# Revit family: Haworth_Lyda_Lounge_Sofa_OneArm
name_source: partatom
category: Furniture
revit_build: Autodesk Revit 2018 (Build: 20170223_1515(x64)
units: mm (PartAtom-declared; Revit-internal decimal feet)

## family parameters
Always vertical = Yes
Cut with Voids When Loaded = No
OmniClass Number = 23.40.70.14.64.21
OmniClass Title = Systems Furniture
Room Calculation Point = No
Shared = No
Work Plane-Based = No

## types (3) — shared parameters
Actual Depth = 32 3/4"
Actual Height = 30 1/4"
Arm Depth = 27"
Arm Height = 12 49/64"
Arm Width = 6 1/4"
Assembly Code = E2020200
Leg Finish = Haworth _ Paint _ Black
Leg Offset = 4 1/2"
Leg Width = 5 119/128"
Manufacturer = Haworth
Revision Number = 1
Seat Depth = 25 3/4"
Seat Height = 17"
Size = Verify Final Dim. w/ Haworth
Standard Depth = 32.75 in
Standard Width = 48.75, 62.75, 90.75 in
Sustainability Info = https://www.haworth.com
URL = www.haworth.com
URL - Product = https://www.haworth.com
Warranty = http://www.haworth.com

## per-type parameters (varying)
| type | Actual Width | Back Upholstery Width | Chair | Description | Drawers | Left Chair | Model | Seat Width | Three Seats | Two Seats |
| Two Seat Sofa | 62 3/4" | 25 1/8" | No | Haworth - Lyda - Lounge - Sofa - Two Seats - w/One Arm | Yes | Yes | HCCL-LYL2-RN | 31 3/8" | No | Yes |
| One Seat Sofa | 48 3/4" | 42 1/2" | Yes | Haworth - Lyda - Lounge - Chair - One Seat - w/One Arm | No | No | HCCL-LYL1-RN | 48 3/4" | No | No |
| Three Seat Sofa | 90 3/4" | 39 1/8" | No | Haworth - Lyda - Lounge - Sofa - Three Seats - w/One Arm | Yes | Yes | HCCL-LYL3-RN | 45 3/8" | Yes | No |

## geometry (parser evidence)
native form markers: Sweep x24
no freeform markers — native parametric forms only
